# Revit family: Tub_Spout-GROHE-Eurosmart-13354XX3_Series
name_source: partatom
category: Plumbing Fixtures
revit_build: Autodesk Revit 2018 (Build: 20170223_1515(x64)
units: mm (PartAtom-declared; Revit-internal decimal feet)

## family parameters
Cut with Voids When Loaded = No
Host = Face
OmniClass Number = 23.45.05.14.21.11
OmniClass Title = Bath/Shower Units
Part Type = Normal
Room Calculation Point = No
Round Connector Dimension = Use Diameter
Shared = Yes

## types (2) — shared parameters
Assembly Code = D2010510
CW Connection = No
CWFU = 3
Default Elevation = 25"
Description = The Eurosmart Tub Spout has a contemporary style crafted to the exacting standards you expect from GROHE. Designed to match the Eurosmart collection, the tub spout is the perfect finishing touch.
HW Connection = No
HWFU = 3
Height = 2 11/16"
IAPMO Compliance = Massachusetts Plumbing Board Approved. CSA B125.1. ASME A112.18.1
Length = 7"
Manufacturer = Grohe
Price = Prices may vary. Please consult Manufacturer Representative for most up-to-date price list.
Product Documentation Link = https://americanstandard.box.com
Product Page URL = https://www.grohe.us
Tempered Connection = Yes
Tempered Water Connection Diameter = 1/2"
Tempered Water Connection Radius = 1/4"
URL = https://www.grohe.us
Vent Connection = No
WFU = 4
Waste Connection = No
Width = 2 11/16"

## per-type parameters (varying)
| type | Finish | Material |
| 13354003 | Brass-Grohe-StarLight Chrome | Brass-Grohe-StarLight Chrome |
| 13354EN3 | Brass-Grohe-Brushed Nickel Infinity Finish | Brass-Grohe-Brushed Nickel Infinity Finish |

note: column(s) folded — value = type name in every type: Model

## geometry (parser evidence)
native form markers: Sweep x3
no freeform markers — native parametric forms only
